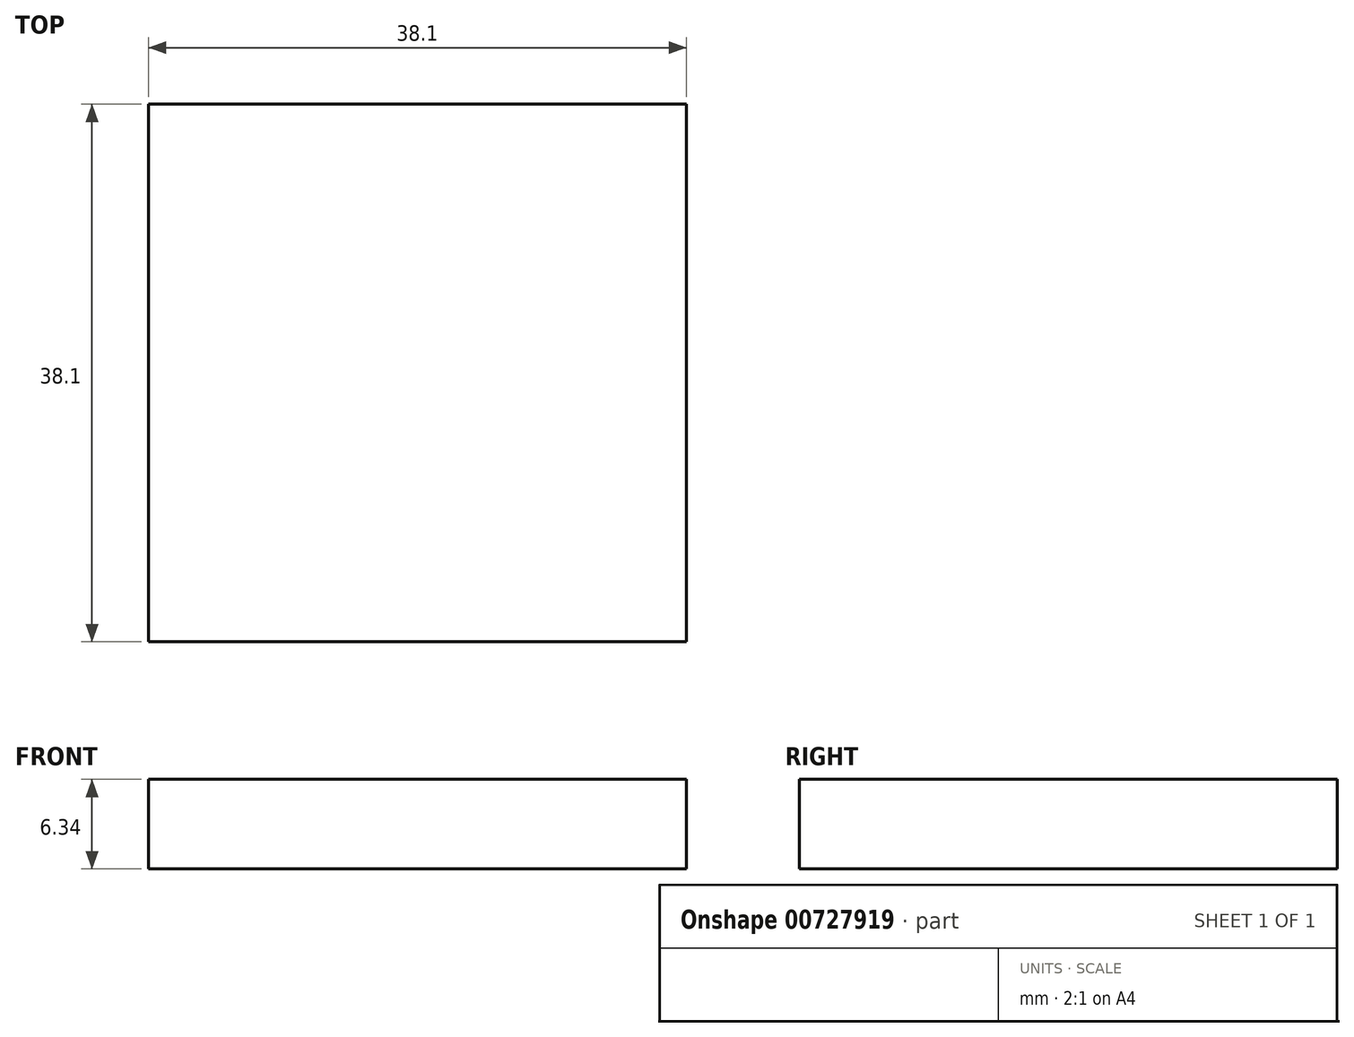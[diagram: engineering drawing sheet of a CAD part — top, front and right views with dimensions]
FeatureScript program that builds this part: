
annotation { "Feature Type Name" : "Feature", "Feature Type Description" : "" }
export const myFeature = defineFeature(function(context is Context, id is Id, definition is map)
    precondition{}
    {
        {
            var Q0;
            Q0=qCreatedBy(makeId("Right.planeOp"),FACE);
            var sketch = newSketch(context, id + "F0", { "sketchPlane" : qUnion([Q0])});
            skLineSegment(sketch, "E0.bottom", {"start": v(27.87, -3.18) * mm, "end": v(-10.23, -3.18) * mm});
            skLineSegment(sketch, "E0.top", {"start": v(27.87, 3.18) * mm, "end": v(-10.23, 3.18) * mm});
            skLineSegment(sketch, "E0.left", {"start": v(27.87, -3.18) * mm, "end": v(27.87, 3.17) * mm});
            skLineSegment(sketch, "E0.right", {"start": v(-10.23, -3.18) * mm, "end": v(-10.23, 3.17) * mm});
            skPoint(sketch, "E0.middle", {"position": v(8.82, 0) * mm});
            skLineSegment(sketch, "E1.bottom", {"start": v(-0.83, 3.18) * mm, "end": v(18.47, 3.18) * mm});
            skLineSegment(sketch, "E1.top", {"start": v(-0.83, 12.32) * mm, "end": v(18.47, 12.32) * mm});
            skLineSegment(sketch, "E1.left", {"start": v(-0.83, 3.17) * mm, "end": v(-0.83, 12.32) * mm});
            skLineSegment(sketch, "E1.right", {"start": v(18.47, 3.17) * mm, "end": v(18.47, 12.32) * mm});
            skSolve(sketch);
        }
        {
            var Q0;
            Q0=makeQuery(id+"F0.imprint","IMPRINT",FACE,{"disambiguationData":[TD([[makeQuery(id+"F0.imprint","IMPRINT",EDGE,{"derivedFrom":sQuery(id+"F0.wireOp",EDGE,"E1.bottom")}),1.0]])]});
            var Q1;
            Q1=makeQuery(id+"F0.imprint","IMPRINT",FACE,{"disambiguationData":[TD([[makeQuery(id+"F0.imprint","IMPRINT",EDGE,{"derivedFrom":sQuery(id+"F0.wireOp",EDGE,"E0.bottom")}),-1.0]])]});
            extrude(context, id + "F1", {"entities" : qUnion([Q0, Q1]), "depth" : 38.1 * mm, "offsetDistance" : 25.4 * mm});
        }
        {
            var Q0;
            Q0=makeQuery(id+"F1.opExtrude","CAP_FACE",FACE,{"disambiguationData":[OSD([sQuery(id+"F0.wireOp",EDGE,"E0.bottom"),sQuery(id+"F0.wireOp",EDGE,"E0.top"),sQuery(id+"F0.wireOp",EDGE,"E0.left"),sQuery(id+"F0.wireOp",EDGE,"E0.right"),sQuery(id+"F0.wireOp",EDGE,"E1.top"),sQuery(id+"F0.wireOp",EDGE,"E1.left"),sQuery(id+"F0.wireOp",EDGE,"E1.right")])],"isStart":false});
            var sketch = newSketch(context, id + "F2", { "sketchPlane" : qUnion([Q0])});
            skCircle(sketch, "E2", {"center": v(8.59, 10.89) * mm, "radius": 6.47 * mm});
            skSolve(sketch);
        }
        {
            var Q0;
            Q0 = qSketchRegion(id + "F2", true);
            extrude(context, id + "F3", {"entities" : qUnion([Q0]), "operationType" : NewBodyOperationType.REMOVE, "oppositeDirection" : true, "depth" : 38.1 * mm, "offsetDistance" : 25.4 * mm});
        }
    });
